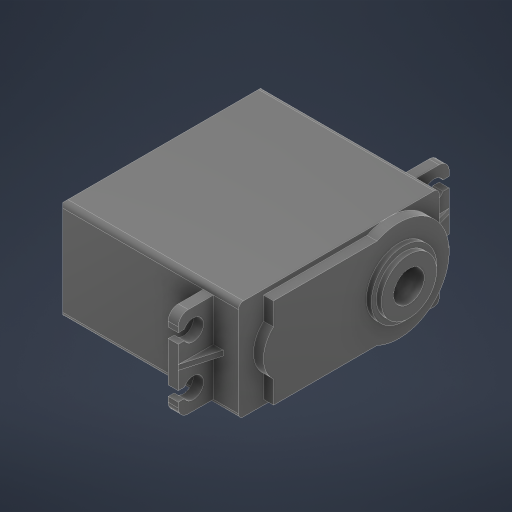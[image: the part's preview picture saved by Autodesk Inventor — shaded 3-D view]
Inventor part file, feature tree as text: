
AUTODESK INVENTOR PART (.ipt)
format: ipt  version: 2023.2 (Build 272271000, 271)  size: 498,176 bytes
history: native  units: mm
features: extrude x9, sketch x3, fillet x2, other x1, chamfer x1, plane x1
ambient origin geometry x8: Origin, YZ Plane, XZ Plane, XY Plane, X Axis, Y Axis, Z Axis, Center Point
bodies: Body1 (feature_tree)
feature tree (17):
  other  "Servo"
  extrude  "Extrusion1"  Depth=40.0mm
  sketch  "Skizze2"  dims[d0=37.0mm d1=40.0mm]
  extrude  "Extrusion2"  Depth=4.0mm
  extrude  "Extrusion3"  Depth=10.0mm
  sketch  "Skizze3"  dims[d2=20.0mm d3=0.0mm d4=4.0mm]
  extrude  "Extrusion4"  Depth=6.0mm
  extrude  "Extrusion5"  Depth=5.0mm TaperAngle=0.0deg
  sketch  "Skizze4"  dims[d5=7.0mm d6=10.0mm d7=6.0mm d8=5.0mm d9=0.0mm d10=2.0mm d11=18.0mm d12=6.0mm d13=54.0mm d14=0.0mm d15=4.1mm d16=4.1mm d17=10.0mm d21=24.0mm d22=4.0mm d23=2.0mm d24=2.0mm d25=0.0mm d26=0.0mm d27=20.0mm d28=10.0mm d29=10.0mm d30=18.0mm d31=5.0mm d32=9.0mm d35=9.0mm d36=4.5mm d38=2.0mm d39=2.0mm d40=0.0mm d41=13.0mm d42=11.0mm d45=10.0mm d46=10.0mm d47=500.0mm d49=360.0deg d51=250.0mm d53=360.0deg d59=1.0mm d60=0.0mm d61=2.0mm d62=0.0mm d63=6.1mm d65=2.0mm d66=2.0mm d67=45.0deg d68=1.0mm d69=2.0mm d70=4.0mm d71=0.0mm d72=7.0mm d73=90.0deg d74=2.0mm d75=3.0mm d76=10.0mm d77=1.0mm d78=0.0mm d79=0.5mm d80=0.872665mm]
  extrude  "Extrusion10"  Depth=2.0mm
  extrude  "Extrusion8"  Depth=18.0mm
  extrude  "Extrusion9"  Depth=6.0mm
  chamfer  "Fase1"  Distance=54.0mm
  fillet  "Rundung2"  Radius=4.1mm
  fillet  "Rundung3"  Radius=4.1mm
  plane  "Arbeitsebene1"
  extrude  "Extrusion11"  Depth=10.0mm
